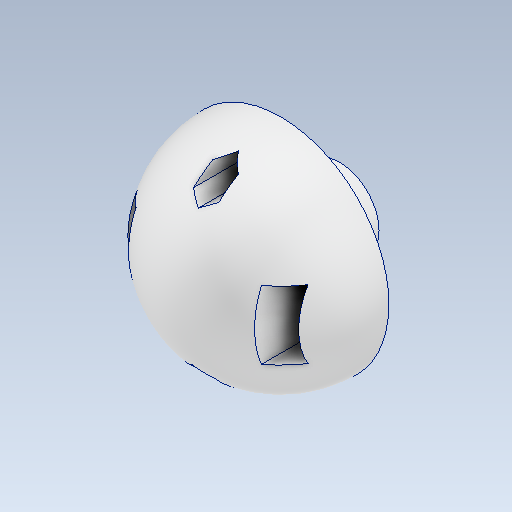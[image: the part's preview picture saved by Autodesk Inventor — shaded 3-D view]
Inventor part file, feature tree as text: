
AUTODESK INVENTOR PART (.ipt)
format: ipt  version: 2021 (Build 250183000, 183)  size: 177,664 bytes
history: native  units: mm
features: sketch x4, other x3
ambient origin geometry x8: Origin, YZ Plane, XZ Plane, XY Plane, X Axis, Y Axis, Z Axis, Center Point
bodies: Solid1 (feature_tree)
feature tree (7):
  other  "Rotatory Hinge 1.ipt"
  other  "Solid1::Rotatory Hinge 1.ipt"
  other  "TaggingFeature1"
  sketch  "Sketch1"  dims[d0=10.0mm]
  sketch  "Sketch2"
  sketch  "Sketch3"
  sketch  "Sketch4"
